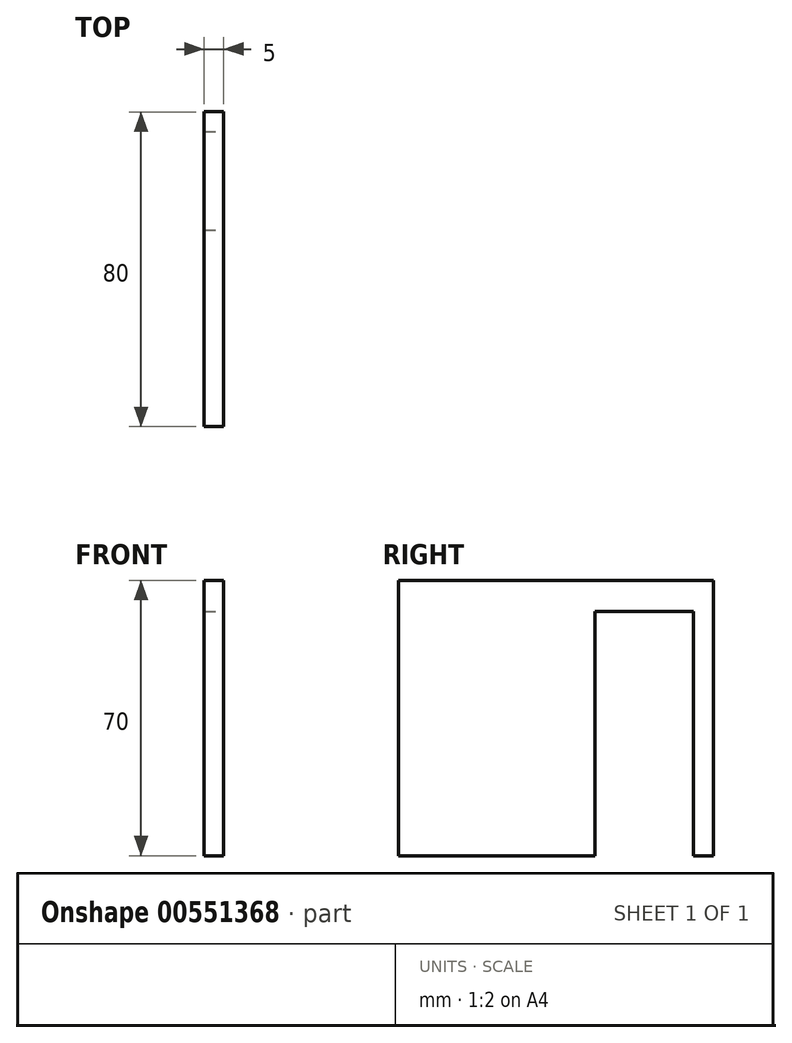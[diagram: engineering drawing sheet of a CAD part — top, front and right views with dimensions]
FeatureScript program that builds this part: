
annotation { "Feature Type Name" : "Feature", "Feature Type Description" : "" }
export const myFeature = defineFeature(function(context is Context, id is Id, definition is map)
    precondition{}
    {
        {
            var Q0;
            Q0=qCreatedBy(makeId("Right.planeOp"),FACE);
            var sketch = newSketch(context, id + "F0", { "sketchPlane" : qUnion([Q0])});
            skLineSegment(sketch, "E0.bottom", {"start": v(-76.26, 42.4) * mm, "end": v(3.74, 42.4) * mm});
            skLineSegment(sketch, "E0.top", {"start": v(-76.26, -27.6) * mm, "end": v(3.74, -27.6) * mm});
            skLineSegment(sketch, "E0.left", {"start": v(-76.26, 42.4) * mm, "end": v(-76.26, -27.6) * mm});
            skLineSegment(sketch, "E0.right", {"start": v(3.74, 42.4) * mm, "end": v(3.74, -27.6) * mm});
            skSolve(sketch);
        }
        {
            var Q0;
            Q0 = qSketchRegion(id + "F0", true);
            extrude(context, id + "F1", {"entities" : qUnion([Q0]), "depth" : 5 * mm, "offsetDistance" : 25 * mm});
        }
        {
            var Q0;
            Q0=makeQuery(id+"F1.opExtrude","CAP_FACE",FACE,{"disambiguationData":[OSD([sQuery(id+"F0.wireOp",EDGE,"E0.bottom"),sQuery(id+"F0.wireOp",EDGE,"E0.top"),sQuery(id+"F0.wireOp",EDGE,"E0.left"),sQuery(id+"F0.wireOp",EDGE,"E0.right")])],"isStart":false});
            var sketch = newSketch(context, id + "F2", { "sketchPlane" : qUnion([Q0])});
            skLineSegment(sketch, "E1.bottom", {"start": v(-26.24, -27.6) * mm, "end": v(-1.24, -27.6) * mm});
            skLineSegment(sketch, "E1.top", {"start": v(-26.24, 34.4) * mm, "end": v(-1.24, 34.4) * mm});
            skLineSegment(sketch, "E1.left", {"start": v(-26.24, -27.6) * mm, "end": v(-26.24, 34.4) * mm});
            skLineSegment(sketch, "E1.right", {"start": v(-1.24, -27.6) * mm, "end": v(-1.24, 34.4) * mm});
            skSolve(sketch);
        }
        {
            var Q0;
            Q0 = qSketchRegion(id + "F2", true);
            extrude(context, id + "F3", {"entities" : qUnion([Q0]), "operationType" : NewBodyOperationType.REMOVE, "oppositeDirection" : true, "depth" : 160 * mm, "offsetDistance" : 25 * mm});
        }
    });
